# Revit family: BE_33032_de_DE
name_source: partatom
category: Leuchten
revit_build: Autodesk Revit 2015 (Build: 20150704_0715(x64)
units: mm (PartAtom-declared; Revit-internal decimal feet)

## types (4) — shared parameters
AC/DC = AC
Aktualisierung = 2016-02-02T04:09:11
BEGA_Dummy = Nein
BEGA_IES = Ja
BEGA_IES1 = Ja
BEGA_IES2 = Ja
BEGA_IES3 = Ja
BEGA_Intern = Ja
BEGA_Intern_Konstruktion = Ja
BEGA_Intern_an = Ja
BEGA_Intern_aus = Ja
Befestigungsabstand = 110 mm
Befestigungsbohrung = Ø 4,5 mm
Beschreibung = Lichtbaustein ®
Beschreibung_Sonderanfertigung = Hier können Sie Informationen zur Sonderanfertigung eintragen.
CE_Konformität = ja
Energieeffizienzklasse = LED A++ - A
Farbfilter = 16777215
Farbtemperaturverschiebung bei Dämpfen der Lampe = <Keine Auswahl>
Farbwiedergabeindex = Ra > 80
Frequenz = 50/60 Hz
Gewicht = 1.05 kg
Hersteller = BEGA
Lampe = LED 4.2 W
Lastklassifizierung = Beleuchtung
Lebensdauerkriterien = L70 = 50.000 h
Logo = BEGA_Logo.png
M_W = Nein
Material_02 = BEGA_Oberfläche_Silber_matt
Material_11 = BEGA_Glas_opal
Neigungswinkel = 0.00°
Produktdatenblatt = http://www.bega.de
Scheinlast = 0 VA
Schutzart = IP 44
Schutzklasse = I
Sonderanfertigung = Nein
Spannung = 0 V
Typenbild = 33032.png
URL = http://www.bega.de
zero-valued in all types: Vorgabe-Ansicht

## per-type parameters (varying)
| type | Bestellnummer | Datei für fotometrisches Netz | Farbtemperatur | LED_Modulbezeichnung | Lampenlichtstrom | Leuchtenlichtstrom | M_A | M_G | Modell |
| BEGA_33032_Grafit_K4 | 33032K4 | BE_33032K4.IES | 4000 K | LED-0261/840 | 525 lm | 322 lm | Nein | Ja | 33032K4 |
| BEGA_33032_Silber_K4 | 33032AK4 | BE_33032K4.IES | 4000 K | LED-0261/840 | 525 lm | 322 lm | Ja | Nein | 33032AK4 |
| BEGA_33032_Silber_K3 | 33032A | BE_33032.IES | 3000 K | LED-0261/830 | 490 lm | 305 lm | Ja | Nein | 33032A |
| BEGA_33032_Grafit_K3 | 33032 | BE_33032.IES | 3000 K | LED-0261/830 | 490 lm | 305 lm | Nein | Ja | 33032 |
